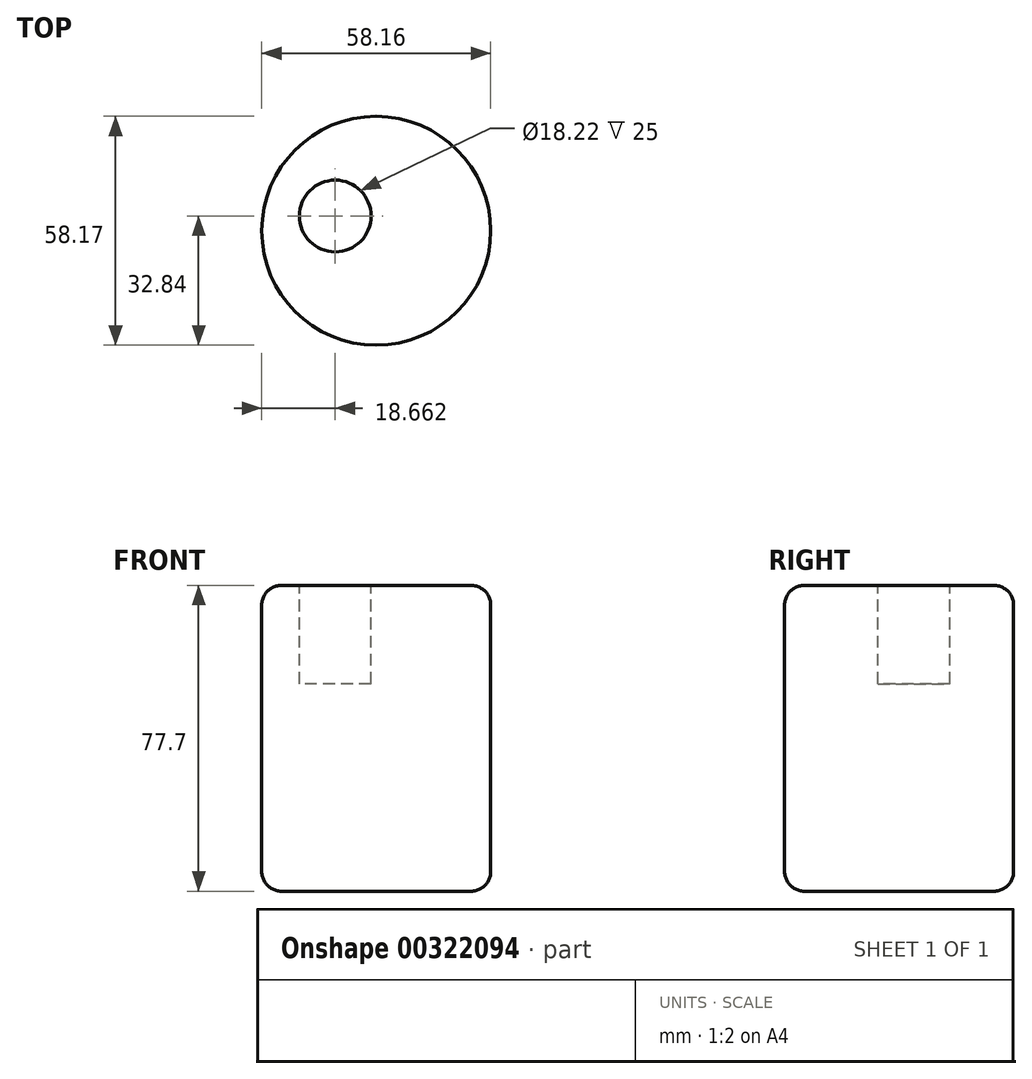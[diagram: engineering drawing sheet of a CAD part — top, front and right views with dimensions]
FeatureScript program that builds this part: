
annotation { "Feature Type Name" : "Feature", "Feature Type Description" : "" }
export const myFeature = defineFeature(function(context is Context, id is Id, definition is map)
    precondition{}
    {
        {
            var Q0;
            Q0=qCreatedBy(makeId("Top.planeOp"),FACE);
            var sketch = newSketch(context, id + "F0", { "sketchPlane" : qUnion([Q0])});
            skCircle(sketch, "E0", {"center": v(0, -3.76) * mm, "radius": 29.08 * mm});
            skSolve(sketch);
        }
        {
            var Q0;
            Q0 = qSketchRegion(id + "F0", true);
            extrude(context, id + "F1", {"entities" : qUnion([Q0]), "depth" : 77.7 * mm});
        }
        {
            var Q0;
            Q0=makeQuery(id+"F1.opExtrude","CAP_FACE",FACE,{"disambiguationData":[OSD([sQuery(id+"F0.wireOp",EDGE,"E0")])],"isStart":false});
            var sketch = newSketch(context, id + "F2", { "sketchPlane" : qUnion([Q0])});
            skCircle(sketch, "E1", {"center": v(-10.42, 0) * mm, "radius": 9.11 * mm});
            skSolve(sketch);
        }
        {
            var Q0;
            Q0 = qSketchRegion(id + "F2", true);
            extrude(context, id + "F3", {"entities" : qUnion([Q0]), "operationType" : NewBodyOperationType.REMOVE, "oppositeDirection" : true, "depth" : 25 * mm});
        }
        {
            var Q0;
            Q0=makeQuery(id+"F1.opExtrude","CAP_EDGE",EDGE,{"disambiguationData":[OSD([sQuery(id+"F0.wireOp",EDGE,"E0")])],"isStart":false});
            var Q1;
            Q1=makeQuery(id+"F1.opExtrude","CAP_EDGE",EDGE,{"disambiguationData":[OSD([sQuery(id+"F0.wireOp",EDGE,"E0")])],"isStart":true});
            fillet(context, id + "F4", {"entities" : qUnion([Q0, Q1]), "radius" : 5 * mm, "tangentPropagation" : true, "allowEdgeOverflow" : false});
        }
    });
